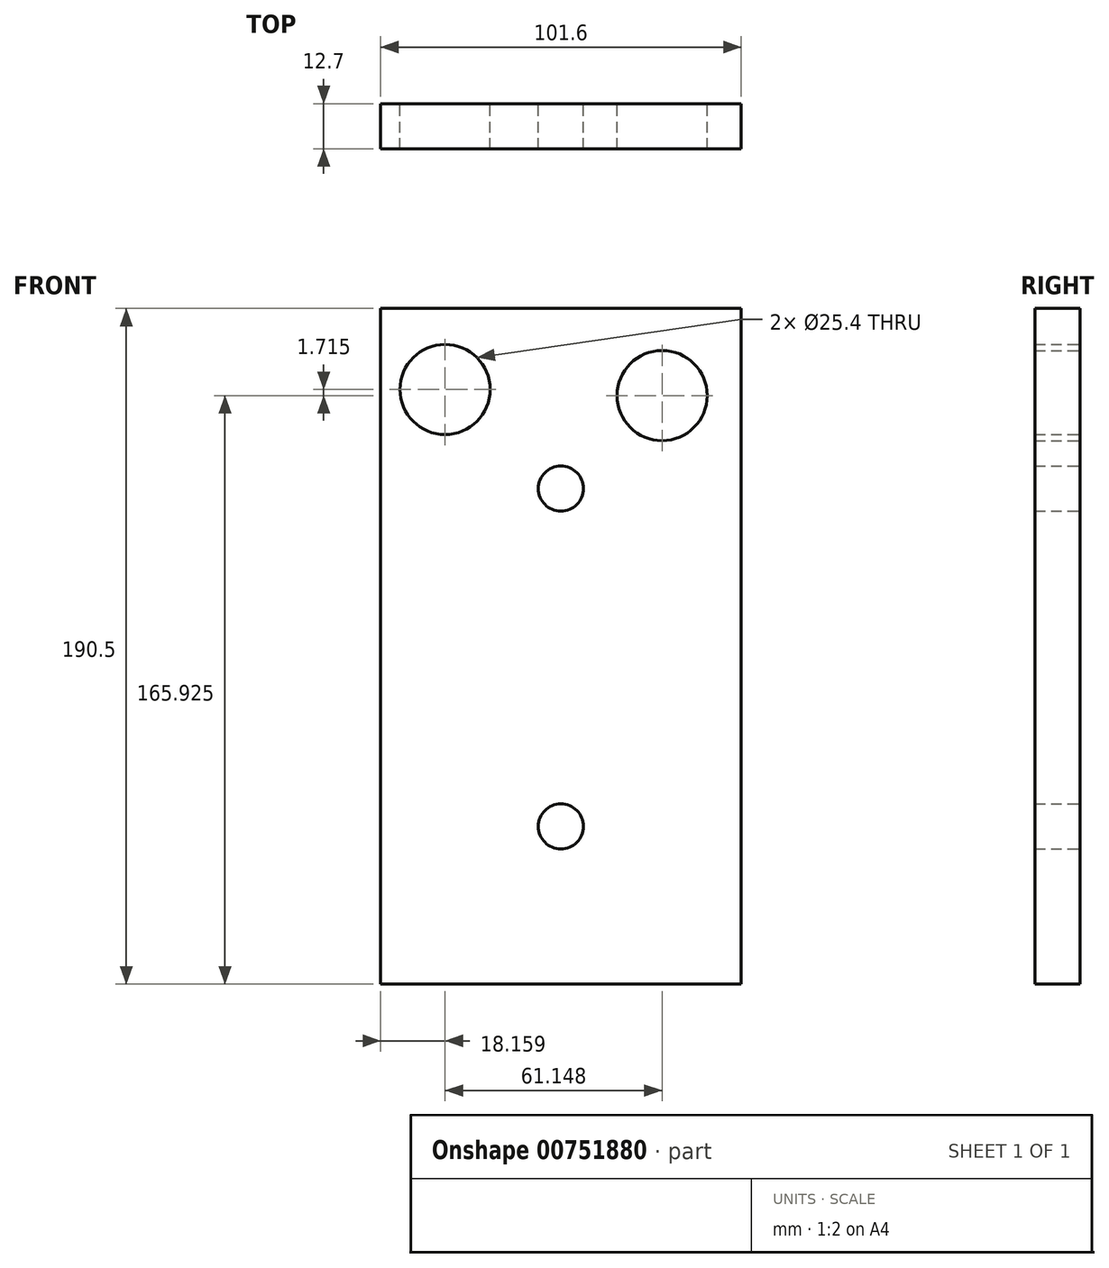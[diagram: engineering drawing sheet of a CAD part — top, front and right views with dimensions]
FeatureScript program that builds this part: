
annotation { "Feature Type Name" : "Feature", "Feature Type Description" : "" }
export const myFeature = defineFeature(function(context is Context, id is Id, definition is map)
    precondition{}
    {
        {
            var Q0;
            Q0=qCreatedBy(makeId("Front.planeOp"),FACE);
            var sketch = newSketch(context, id + "F0", { "sketchPlane" : qUnion([Q0])});
            skLineSegment(sketch, "E0.bottom", {"start": v(-50.8, 88.9) * mm, "end": v(50.8, 88.9) * mm});
            skLineSegment(sketch, "E0.top", {"start": v(-50.8, -88.9) * mm, "end": v(50.8, -88.9) * mm});
            skLineSegment(sketch, "E0.left", {"start": v(-50.8, 88.9) * mm, "end": v(-50.8, -88.9) * mm});
            skLineSegment(sketch, "E0.right", {"start": v(50.8, 88.9) * mm, "end": v(50.8, -88.9) * mm});
            skPoint(sketch, "E0.middle", {"position": v(0, 0) * mm});
            skSolve(sketch);
        }
        {
            var Q0;
            Q0=makeQuery(id+"F0.imprint","IMPRINT",FACE,{"disambiguationData":[TD([[makeQuery(id+"F0.imprint","IMPRINT",EDGE,{"derivedFrom":sQuery(id+"F0.wireOp",EDGE,"E0.bottom")}),-1.0]])]});
            extrude(context, id + "F1", {"entities" : qUnion([Q0]), "depth" : 12.7 * mm, "offsetDistance" : 25.4 * mm});
        }
        {
            var Q0;
            Q0=makeQuery(id+"F1.opExtrude","SWEPT_FACE",FACE,{"disambiguationData":[OSD([sQuery(id+"F0.wireOp",EDGE,"E0.top")])]});
            var sketch = newSketch(context, id + "F2", { "sketchPlane" : qUnion([Q0])});
            skLineSegment(sketch, "E1.bottom", {"start": v(0, 6.35) * mm, "end": v(0, 6.35) * mm});
            skLineSegment(sketch, "E1.top", {"start": v(0, 6.35) * mm, "end": v(0, 6.35) * mm});
            skLineSegment(sketch, "E1.left", {"start": v(0, 6.35) * mm, "end": v(0, 6.35) * mm});
            skLineSegment(sketch, "E1.right", {"start": v(0, 6.35) * mm, "end": v(0, 6.35) * mm});
            skPoint(sketch, "E1.middle", {"position": v(0, 6.35) * mm});
            skPoint(sketch, "E1.middle.positionSnap0", {"position": v(0, 12.7) * mm});
            skPoint(sketch, "E1.middle.positionSnap1", {"position": v(-50.8, 6.35) * mm});
            skPoint(sketch, "E1.centerSnap0", {"position": v(0, 12.7) * mm});
            skPoint(sketch, "E1.centerSnap1", {"position": v(-50.8, 6.35) * mm});
            skSolve(sketch);
        }
        {
            var Q0;
            {var subQ0=sQuery(id+"F2.wireOp",EDGE,"E1.top");Q0=makeQuery(id+"F2.imprint","IMPRINT",FACE,{"disambiguationData":[TD([[makeQuery(id+"F2.imprint","IMPRINT",EDGE,{"derivedFrom":subQ0}),-1.0]])]});}
            var Q1;
            {var subQ0=sQuery(id+"F2.wireOp",EDGE,"E1.bottom");Q1=makeQuery(id+"F2.imprint","IMPRINT",FACE,{"disambiguationData":[TD([[makeQuery(id+"F2.imprint","IMPRINT",EDGE,{"derivedFrom":subQ0}),1.0]])]});}
            var Q2;
            {var subQ1=sQuery(id+"F0.wireOp",EDGE,"E0.top");var subQ2=makeQuery(id+"F1.opExtrude","CAP_EDGE",EDGE,{"disambiguationData":[OSD([subQ1])],"isStart":true});Q2=makeQuery(id+"F2.imprint","IMPRINT",FACE,{"disambiguationData":[TD([[makeQuery(id+"F2.imprint","IMPRINT",EDGE,{"derivedFrom":subQ2}),1.0]])]});}
            extrude(context, id + "F3", {"entities" : qUnion([Q0, Q1, Q2]), "operationType" : NewBodyOperationType.ADD, "depth" : 12.7 * mm, "offsetDistance" : 25.4 * mm});
        }
        {
            var Q0;
            Q0=makeQuery(id+"F1.opExtrude","CAP_FACE",FACE,{"disambiguationData":[OSD([sQuery(id+"F0.wireOp",EDGE,"E0.bottom"),sQuery(id+"F0.wireOp",EDGE,"E0.top"),sQuery(id+"F0.wireOp",EDGE,"E0.left"),sQuery(id+"F0.wireOp",EDGE,"E0.right")])],"isStart":true});
            var sketch = newSketch(context, id + "F4", { "sketchPlane" : qUnion([Q0])});
            skCircle(sketch, "E2", {"center": v(0, 38.1) * mm, "radius": 6.35 * mm});
            skCircle(sketch, "E3", {"center": v(-28.5, 64.32) * mm, "radius": 12.7 * mm});
            skCircle(sketch, "E4", {"center": v(32.64, 66.04) * mm, "radius": 12.7 * mm});
            skSolve(sketch);
        }
        {
            var Q0;
            Q0=makeQuery(id+"F4.imprint","IMPRINT",FACE,{"disambiguationData":[TD([[makeQuery(id+"F4.imprint","IMPRINT",EDGE,{"derivedFrom":sQuery(id+"F4.wireOp",EDGE,"E3")}),1.0]])]});
            var Q1;
            Q1=makeQuery(id+"F4.imprint","IMPRINT",FACE,{"disambiguationData":[TD([[makeQuery(id+"F4.imprint","IMPRINT",EDGE,{"derivedFrom":sQuery(id+"F4.wireOp",EDGE,"E2")}),1.0]])]});
            var Q2;
            Q2=makeQuery(id+"F4.imprint","IMPRINT",FACE,{"disambiguationData":[TD([[makeQuery(id+"F4.imprint","IMPRINT",EDGE,{"derivedFrom":sQuery(id+"F4.wireOp",EDGE,"E4")}),1.0]])]});
            extrude(context, id + "F5", {"entities" : qUnion([Q0, Q1, Q2]), "operationType" : NewBodyOperationType.REMOVE, "endBound" : BoundingType.THROUGH_ALL, "oppositeDirection" : true, "depth" : 25.4 * mm, "offsetDistance" : 25.4 * mm});
        }
        {
            var Q0;
            Q0=makeQuery(id+"F1.opExtrude","CAP_FACE",FACE,{"disambiguationData":[OSD([sQuery(id+"F0.wireOp",EDGE,"E0.bottom"),sQuery(id+"F0.wireOp",EDGE,"E0.top"),sQuery(id+"F0.wireOp",EDGE,"E0.left"),sQuery(id+"F0.wireOp",EDGE,"E0.right")])],"isStart":true});
            var sketch = newSketch(context, id + "F6", { "sketchPlane" : qUnion([Q0])});
            skCircle(sketch, "E5", {"center": v(0, -57.15) * mm, "radius": 6.35 * mm});
            skSolve(sketch);
        }
        {
            var Q0;
            Q0=makeQuery(id+"F6.imprint","IMPRINT",FACE,{"disambiguationData":[TD([[makeQuery(id+"F6.imprint","IMPRINT",EDGE,{"derivedFrom":sQuery(id+"F6.wireOp",EDGE,"E5")}),1.0]])]});
            extrude(context, id + "F7", {"entities" : qUnion([Q0]), "operationType" : NewBodyOperationType.REMOVE, "endBound" : BoundingType.THROUGH_ALL, "oppositeDirection" : true, "depth" : 25.4 * mm, "offsetDistance" : 25.4 * mm});
        }
    });
